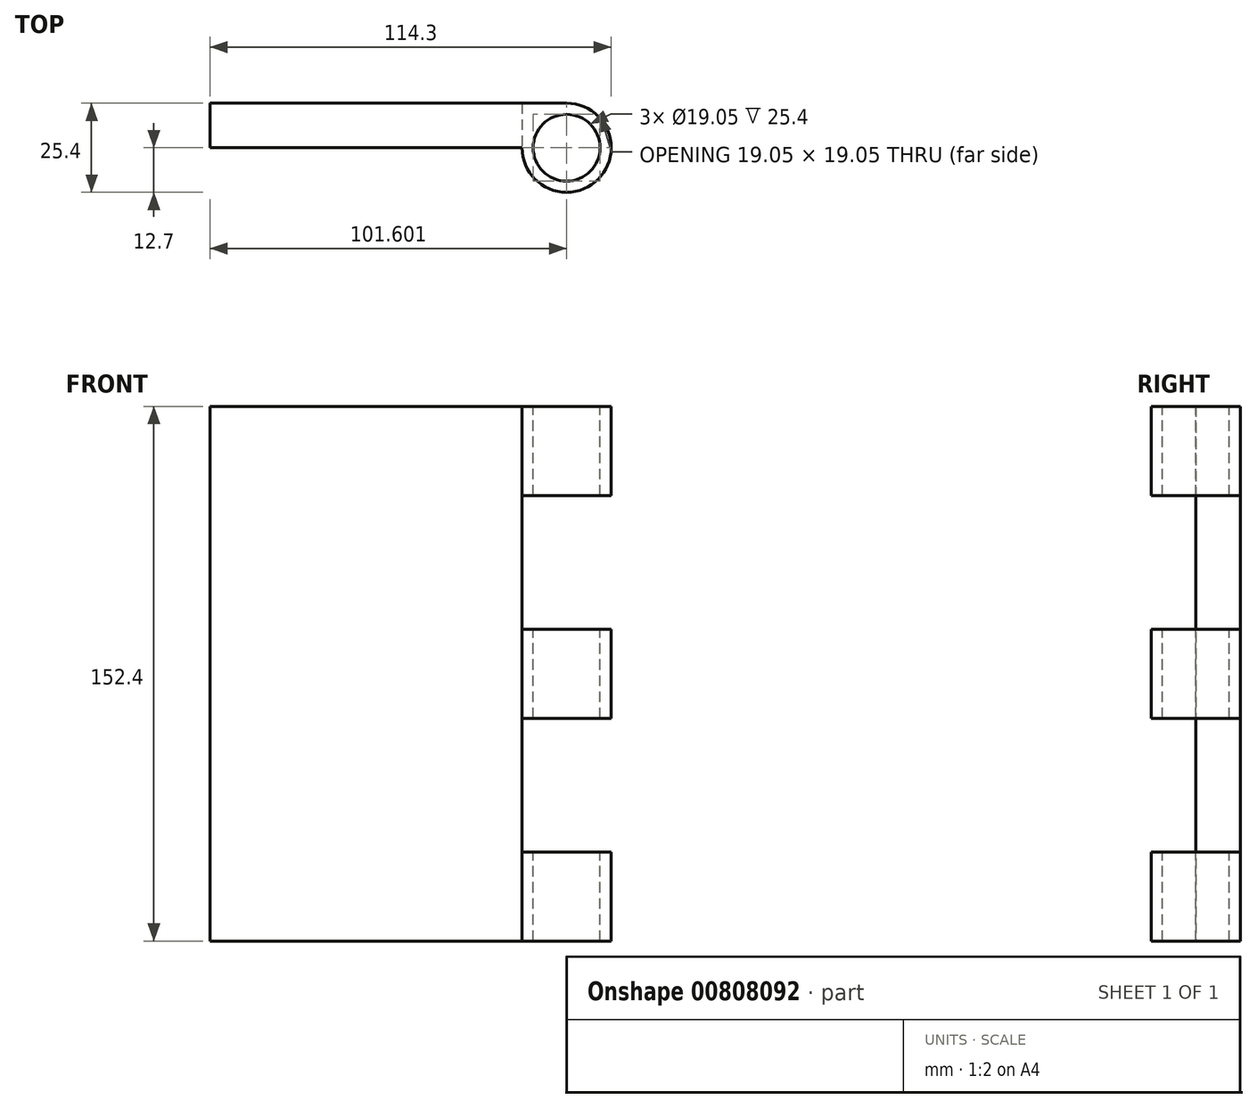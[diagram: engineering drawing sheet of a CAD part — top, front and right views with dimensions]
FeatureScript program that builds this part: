
annotation { "Feature Type Name" : "Feature", "Feature Type Description" : "" }
export const myFeature = defineFeature(function(context is Context, id is Id, definition is map)
    precondition{}
    {
        {
            var Q0;
            Q0=qCreatedBy(makeId("Front.planeOp"),FACE);
            var sketch = newSketch(context, id + "F0", { "sketchPlane" : qUnion([Q0])});
            skLineSegment(sketch, "E0.bottom", {"start": v(-39.5, 77.5) * mm, "end": v(62.1, 77.5) * mm});
            skLineSegment(sketch, "E0.top", {"start": v(-39.5, -74.9) * mm, "end": v(62.1, -74.9) * mm});
            skLineSegment(sketch, "E0.left", {"start": v(-39.5, 77.5) * mm, "end": v(-39.5, -74.9) * mm});
            skLineSegment(sketch, "E0.right", {"start": v(62.1, 77.5) * mm, "end": v(62.1, -74.9) * mm});
            skSolve(sketch);
        }
        {
            var Q0;
            Q0=makeQuery(id+"F0.imprint","IMPRINT",FACE,{"disambiguationData":[TD([[makeQuery(id+"F0.imprint","IMPRINT",EDGE,{"derivedFrom":sQuery(id+"F0.wireOp",EDGE,"E0.bottom")}),-1.0]])]});
            extrude(context, id + "F1", {"entities" : qUnion([Q0]), "depth" : 12.7 * mm, "offsetDistance" : 25.4 * mm});
        }
        {
            var Q0;
            Q0=makeQuery(id+"F1.opExtrude","SWEPT_FACE",FACE,{"disambiguationData":[OSD([sQuery(id+"F0.wireOp",EDGE,"E0.bottom")])]});
            var sketch = newSketch(context, id + "F2", { "sketchPlane" : qUnion([Q0])});
            skCircle(sketch, "E1", {"center": v(62.1, -12.7) * mm, "radius": 12.7 * mm});
            skSolve(sketch);
        }
        {
            var Q0;
            Q0=makeQuery(id+"F2.imprint","IMPRINT",FACE,{"disambiguationData":[TD([[makeQuery(id+"F2.imprint","IMPRINT",EDGE,{"derivedFrom":sQuery(id+"F2.wireOp",EDGE,"AtYBVnGq-jbLN-iIk4-UTEE-TkR76Q6qanXP")}),1.0]])]});
            var Q1;
            {var subQ1=sQuery(id+"F0.wireOp",EDGE,"E0.bottom");var subQ2=makeQuery(id+"F1.opExtrude","SWEPT_EDGE",EDGE,{"disambiguationData":[OSD([subQ1,sQuery(id+"F0.wireOp",EDGE,"E0.right")])]});Q1=makeQuery(id+"F2.imprint","IMPRINT",FACE,{"disambiguationData":[TD([[makeQuery(id+"F2.imprint","IMPRINT",EDGE,{"derivedFrom":subQ2}),-1.0]])]});}
            extrude(context, id + "F3", {"entities" : qUnion([Q0, Q1]), "operationType" : NewBodyOperationType.ADD, "oppositeDirection" : true, "depth" : 152.4 * mm, "offsetDistance" : 25.4 * mm});
        }
        {
            var Q0;
            {var subQ0=sQuery(id+"F0.wireOp",EDGE,"E0.bottom");Q0=makeQuery(id+"F3.boolean.opBoolean","MERGE",FACE,{"derivedFrom":[makeQuery(id+"F1.opExtrude","SWEPT_FACE",FACE,{"disambiguationData":[OSD([subQ0])]}),makeQuery(id+"F3.opExtrude","CAP_FACE",FACE,{"disambiguationData":[OSD([subQ0,sQuery(id+"F0.wireOp",EDGE,"E0.right"),sQuery(id+"F2.wireOp",EDGE,"AtYBVnGq-jbLN-iIk4-UTEE-TkR76Q6qanXP")])],"isStart":true})]});}
            var sketch = newSketch(context, id + "F4", { "sketchPlane" : qUnion([Q0])});
            skPoint(sketch, "E2", {"position": v(62.1, -12.7) * mm});
            skCircle(sketch, "E3", {"center": v(62.1, -12.7) * mm, "radius": 9.53 * mm});
            skSolve(sketch);
        }
        {
            var Q0;
            Q0=makeQuery(id+"F4.imprint","IMPRINT",FACE,{"disambiguationData":[TD([[makeQuery(id+"F4.imprint","IMPRINT",EDGE,{"derivedFrom":sQuery(id+"F4.wireOp",EDGE,"E3")}),1.0]])]});
            extrude(context, id + "F5", {"entities" : qUnion([Q0]), "operationType" : NewBodyOperationType.REMOVE, "endBound" : BoundingType.UP_TO_NEXT, "oppositeDirection" : true, "depth" : 25.4 * mm, "offsetDistance" : 25.4 * mm});
        }
        {
            var Q0;
            Q0=qCreatedBy(makeId("Front.planeOp"),FACE);
            cPlane(context, id + "F6", {"entities" : qUnion([Q0]), "cplaneType" : CPlaneType.OFFSET, "offset" : 25.4 * mm, "width" : 152.4 * mm, "height" : 152.4 * mm});
        }
        {
            var Q0;
            Q0=qCreatedBy(id+"F6.planeOp",FACE);
            var sketch = newSketch(context, id + "F7", { "sketchPlane" : qUnion([Q0])});
            skLineSegment(sketch, "E4.0", {"start": v(49.4, 77.5) * mm, "end": v(49.4, -74.9) * mm, "construction": true});
            skLineSegment(sketch, "E5.bottom", {"start": v(49.4, 52.1) * mm, "end": v(100.2, 52.1) * mm});
            skLineSegment(sketch, "E5.top", {"start": v(49.4, 14) * mm, "end": v(100.2, 14) * mm});
            skLineSegment(sketch, "E5.left", {"start": v(49.4, 52.1) * mm, "end": v(49.4, 14) * mm});
            skLineSegment(sketch, "E5.right", {"start": v(100.2, 52.1) * mm, "end": v(100.2, 14) * mm});
            skLineSegment(sketch, "E6.bottom", {"start": v(49.4, -11.4) * mm, "end": v(100.2, -11.4) * mm});
            skLineSegment(sketch, "E6.top", {"start": v(49.4, -49.5) * mm, "end": v(100.2, -49.5) * mm});
            skLineSegment(sketch, "E6.left", {"start": v(49.4, -11.4) * mm, "end": v(49.4, -49.5) * mm});
            skLineSegment(sketch, "E6.right", {"start": v(100.2, -11.4) * mm, "end": v(100.2, -49.5) * mm});
            skSolve(sketch);
        }
        {
            var Q0;
            Q0=makeQuery(id+"F7.imprint","IMPRINT",FACE,{"disambiguationData":[TD([[makeQuery(id+"F7.imprint","IMPRINT",EDGE,{"derivedFrom":sQuery(id+"F7.wireOp",EDGE,"E5.bottom")}),-1.0]])]});
            var Q1;
            Q1=makeQuery(id+"F7.imprint","IMPRINT",FACE,{"disambiguationData":[TD([[makeQuery(id+"F7.imprint","IMPRINT",EDGE,{"derivedFrom":sQuery(id+"F7.wireOp",EDGE,"E6.bottom")}),-1.0]])]});
            extrude(context, id + "F8", {"entities" : qUnion([Q0, Q1]), "operationType" : NewBodyOperationType.REMOVE, "oppositeDirection" : true, "depth" : 50.8 * mm, "offsetDistance" : 25.4 * mm});
        }
    });
